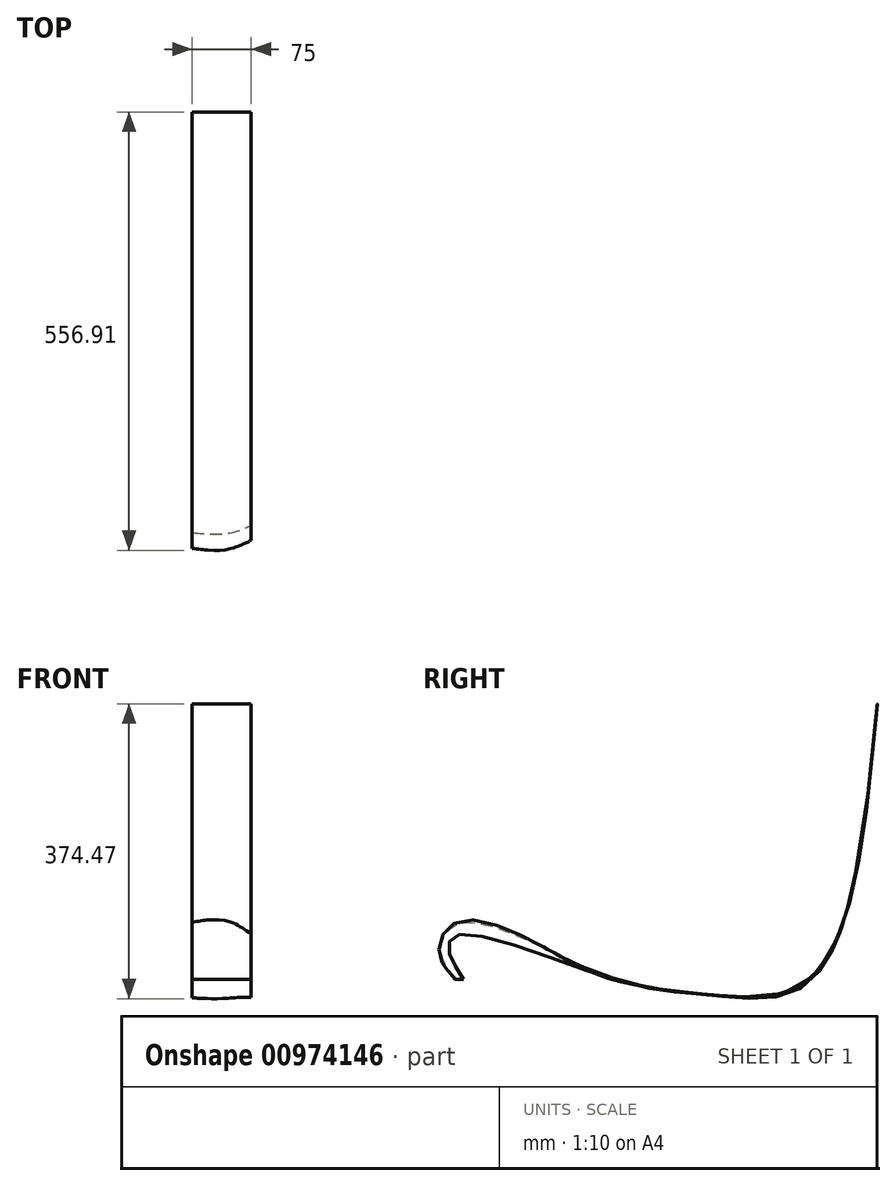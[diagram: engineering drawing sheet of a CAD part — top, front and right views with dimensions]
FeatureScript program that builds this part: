
annotation { "Feature Type Name" : "Feature", "Feature Type Description" : "" }
export const myFeature = defineFeature(function(context is Context, id is Id, definition is map)
    precondition{}
    {
        {
            var Q0;
            Q0=qCreatedBy(makeId("Right.planeOp"),FACE);
            var sketch = newSketch(context, id + "F0", { "sketchPlane" : qUnion([Q0])});
            skLineSegment(sketch, "E0", {"start": v(0, 0) * mm, "end": v(-200, 0) * mm});
            skLineSegment(sketch, "E1", {"start": v(-200, 0) * mm, "end": v(250, 0) * mm});
            skLineSegment(sketch, "E2", {"start": v(250, 0) * mm, "end": v(250, 350) * mm});
            skLineSegment(sketch, "E3", {"start": v(-200, 0) * mm, "end": v(-200, 70) * mm});
            skLineSegment(sketch, "E4", {"start": v(250, 0) * mm, "end": v(0, 0) * mm});
            skLineSegment(sketch, "E5", {"start": v(250, 350) * mm, "end": v(290, 350) * mm});
            skLineSegment(sketch, "E6", {"start": v(-200, 35) * mm, "end": v(-240, 35) * mm});
            skPoint(sketch, "E7.4.internal.snap0", {"position": v(125, 0) * mm});
            skLineSegment(sketch, "E8", {"start": v(-240, 35) * mm, "end": v(-220, 35) * mm});
            skLineSegment(sketch, "E9", {"start": v(-200, 0) * mm, "end": v(-100, 0) * mm});
            skLineSegment(sketch, "E10", {"start": v(-100, 0) * mm, "end": v(-100, 45) * mm});
            skLineSegment(sketch, "E11", {"start": v(125, 0) * mm, "end": v(125, -20) * mm});
            skFitSpline(sketch, "E12", {"points": [v(-200, 0) * mm, v(-220, 35) * mm, v(-200, 70) * mm, v(-100, 45) * mm, v(0, 0) * mm, v(125, -20) * mm, v(250, 0) * mm, v(334.24, 350) * mm], "startDerivative": vector(-331.59, 382.06) * mm, "endDerivative": vector(171.14, 1772.4) * mm});
            skSolve(sketch);
        }
        {
            var Q0;
            Q0=qCreatedBy(makeId("Right.planeOp"),FACE);
            cPlane(context, id + "F1", {"entities" : qUnion([Q0]), "cplaneType" : CPlaneType.OFFSET, "offset" : 50 * mm, "width" : 150 * mm, "height" : 150 * mm});
        }
        {
            var Q0;
            Q0=qCreatedBy(id+"F1.planeOp",FACE);
            var sketch = newSketch(context, id + "F2", { "sketchPlane" : qUnion([Q0])});
            skFitSpline(sketch, "E13", {"points": [v(-200.1, 0) * mm, v(-220.1, 35) * mm, v(-200.1, 70) * mm, v(-100.1, 45) * mm, v(-0.1, 0) * mm, v(124.9, -20) * mm, v(249.9, 0) * mm, v(334.14, 350) * mm], "startDerivative": vector(-331.59, 382.06) * mm, "endDerivative": vector(171.14, 1772.4) * mm});
            skSolve(sketch);
        }
        {
            var Q0;
            Q0=qCreatedBy(id+"F1.planeOp",FACE);
            cPlane(context, id + "F3", {"entities" : qUnion([Q0]), "cplaneType" : CPlaneType.OFFSET, "offset" : 25 * mm, "width" : 150 * mm, "height" : 150 * mm});
        }
        {
            var Q0;
            Q0=qCreatedBy(id+"F3.planeOp",FACE);
            var sketch = newSketch(context, id + "F4", { "sketchPlane" : qUnion([Q0])});
            skFitSpline(sketch, "E14", {"points": [v(-191.24, 0) * mm, v(-209.63, 35.32) * mm, v(-199.82, 56.58) * mm, v(0, 0) * mm, v(124.8, -19.87) * mm, v(248.74, 0) * mm, v(334.13, 350.01) * mm], "startDerivative": vector(-256.68, 373.76) * mm, "endDerivative": vector(146.17, 1591.24) * mm});
            skSolve(sketch);
        }
        {
            var Q0;
            Q0=qCreatedBy(makeId("Right.planeOp"),FACE);
            cPlane(context, id + "F5", {"entities" : qUnion([Q0]), "cplaneType" : CPlaneType.OFFSET, "offset" : 80 * mm, "width" : 150 * mm, "height" : 150 * mm});
        }
        {
            var Q0;
            Q0=sQuery(id+"F0.wireOp",EDGE,"E12");
            var Q1;
            Q1=sQuery(id+"F2.wireOp",EDGE,"E13");
            var Q2;
            Q2=sQuery(id+"F4.wireOp",EDGE,"E14");
            loft(context, id + "F6", {"bodyType" : ToolBodyType.SURFACE, "wireProfilesArray" : [{ "wireProfileEntities" : qUnion([Q0]) }, { "wireProfileEntities" : qUnion([Q1]) }, { "wireProfileEntities" : qUnion([Q2]) }]});
        }
    });
